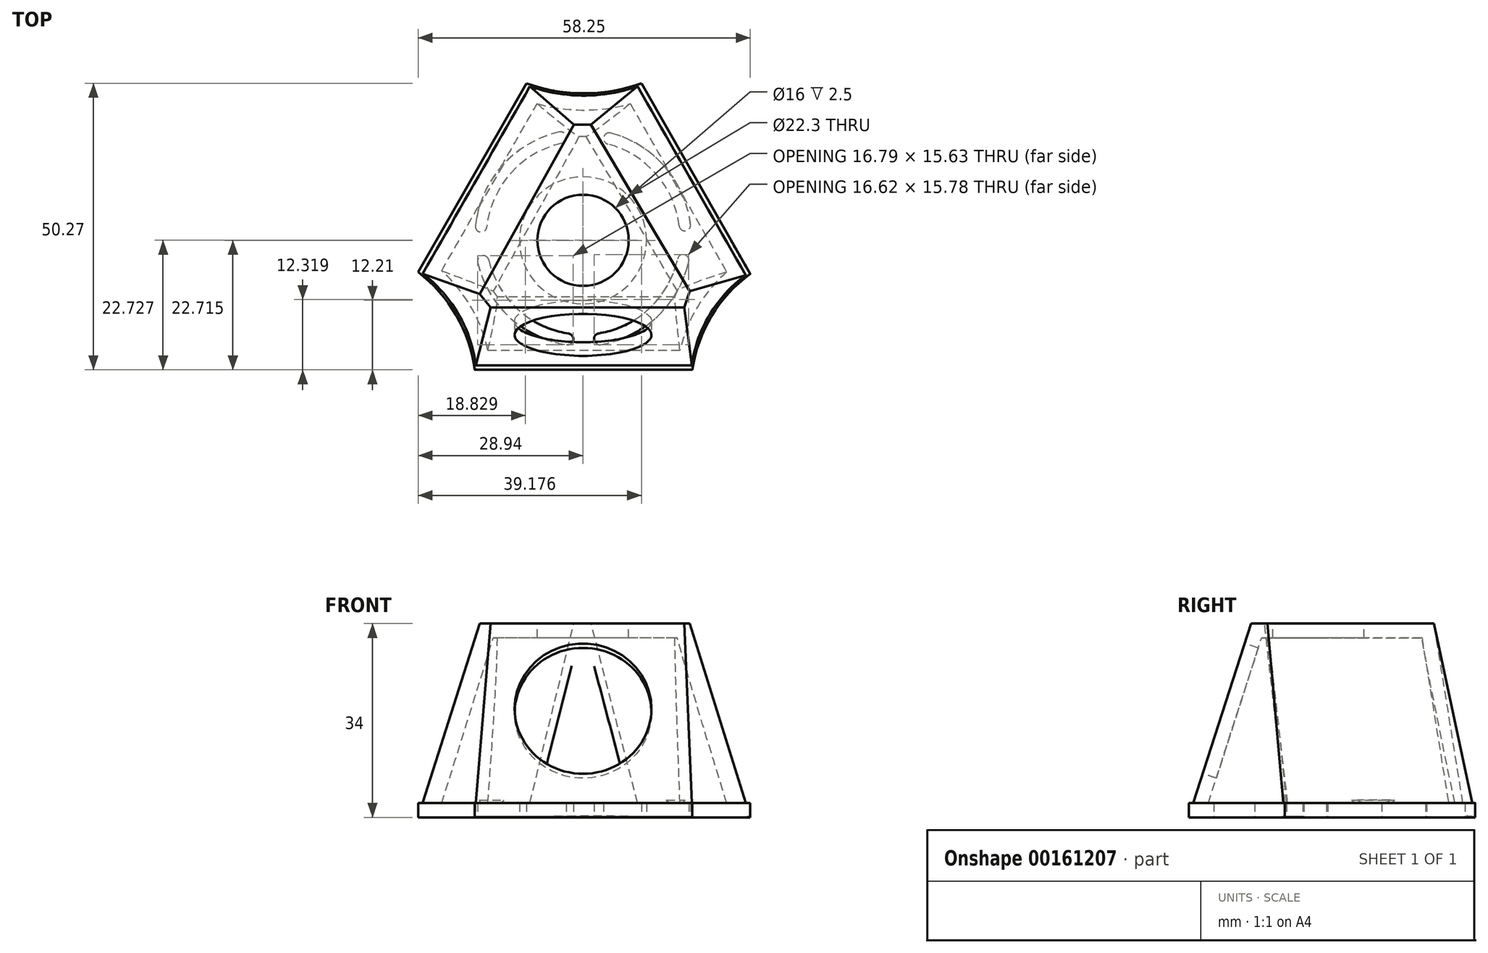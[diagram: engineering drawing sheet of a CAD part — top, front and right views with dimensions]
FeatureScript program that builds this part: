
annotation { "Feature Type Name" : "Feature", "Feature Type Description" : "" }
export const myFeature = defineFeature(function(context is Context, id is Id, definition is map)
    precondition{}
    {
        {
            var Q0;
            Q0=qCreatedBy(makeId("Top.planeOp"),FACE);
            cPlane(context, id + "F0", {"entities" : qUnion([Q0]), "cplaneType" : CPlaneType.OFFSET, "offset" : 34 * mm, "width" : 150 * mm, "height" : 150 * mm});
        }
        {
            var Q0;
            Q0=qCreatedBy(makeId("Top.planeOp"),FACE);
            var sketch = newSketch(context, id + "F1", { "sketchPlane" : qUnion([Q0])});
            skLineSegment(sketch, "E0", {"start": v(-28.93, -4.72) * mm, "end": v(-9.95, 28.39) * mm});
            skLineSegment(sketch, "E1", {"start": v(10.22, 28.39) * mm, "end": v(29.31, -5.05) * mm});
            skLineSegment(sketch, "E2", {"start": v(19.17, -21.87) * mm, "end": v(-19, -21.87) * mm});
            skArc(sketch, "E3", {"start": v(-9.95, 28.39) * mm, "mid": v(0.14, 26.64) * mm, "end": v(10.22, 28.39) * mm});
            skArc(sketch, "E4", {"start": v(-19, -21.87) * mm, "mid": v(-22.22, -12.29) * mm, "end": v(-28.93, -4.72) * mm});
            skArc(sketch, "E5", {"start": v(29.31, -5.05) * mm, "mid": v(22.5, -12.41) * mm, "end": v(19.17, -21.87) * mm});
            skSolve(sketch);
        }
        {
            var Q0;
            Q0=qCreatedBy(id+"F0.planeOp",FACE);
            var sketch = newSketch(context, id + "F2", { "sketchPlane" : qUnion([Q0])});
            skLineSegment(sketch, "E6", {"start": v(-18.1, -8.57) * mm, "end": v(-1.61, 21.16) * mm});
            skLineSegment(sketch, "E7", {"start": v(-1.61, 21.16) * mm, "end": v(1.39, 21.16) * mm});
            skLineSegment(sketch, "E8", {"start": v(1.39, 21.16) * mm, "end": v(18.72, -8.08) * mm});
            skLineSegment(sketch, "E9", {"start": v(18.72, -8.08) * mm, "end": v(17.75, -10.92) * mm});
            skLineSegment(sketch, "E10", {"start": v(17.75, -10.92) * mm, "end": v(-16.25, -10.92) * mm});
            skLineSegment(sketch, "E11", {"start": v(-16.25, -10.92) * mm, "end": v(-18.1, -8.57) * mm});
            skSolve(sketch);
        }
        {
            var Q0;
            Q0=makeQuery(id+"F1.imprint","IMPRINT",FACE,{"disambiguationData":[TD([[makeQuery(id+"F1.imprint","IMPRINT",EDGE,{"derivedFrom":sQuery(id+"F1.wireOp",EDGE,"E0")}),-1.0]])]});
            var Q1;
            Q1=makeQuery(id+"F2.imprint","IMPRINT",FACE,{"disambiguationData":[TD([[makeQuery(id+"F2.imprint","IMPRINT",EDGE,{"derivedFrom":sQuery(id+"F2.wireOp",EDGE,"E6")}),-1.0]])]});
            loft(context, id + "F3", {"sheetProfilesArray" : [{ "sheetProfileEntities" : qUnion([Q0]) }, { "sheetProfileEntities" : qUnion([Q1]) }]});
        }
        {
            var Q0;
            Q0=makeQuery(id+"F3.opLoft","CAP_FACE",FACE,{"disambiguationData":[OSD([makeQuery(id+"F1.imprint","IMPRINT",FACE,{"disambiguationData":[TD([[makeQuery(id+"F1.imprint","IMPRINT",EDGE,{"derivedFrom":sQuery(id+"F1.wireOp",EDGE,"E0")}),-1.0]])]})])],"isStart":true});
            shell(context, id + "F4", {"entities" : qUnion([Q0]), "thickness" : 2.5 * mm});
        }
        {
            var Q0;
            Q0=qCreatedBy(makeId("Top.planeOp"),FACE);
            var sketch = newSketch(context, id + "F5", { "sketchPlane" : qUnion([Q0])});
            skCircle(sketch, "E12", {"center": v(0, 0.84) * mm, "radius": 11.15 * mm});
            skSolve(sketch);
        }
        {
            var Q0;
            Q0=qCreatedBy(id+"F0.planeOp",FACE);
            var sketch = newSketch(context, id + "F6", { "sketchPlane" : qUnion([Q0])});
            skCircle(sketch, "E13", {"center": v(0, 0.86) * mm, "radius": 8 * mm});
            skSolve(sketch);
        }
        {
            var Q0;
            Q0 = qSketchRegion(id + "F6", true);
            extrude(context, id + "F7", {"entities" : qUnion([Q0]), "operationType" : NewBodyOperationType.REMOVE, "endBound" : BoundingType.UP_TO_NEXT, "oppositeDirection" : true, "depth" : 25 * mm});
        }
        {
            var Q0;
            Q0=qCreatedBy(makeId("Top.planeOp"),FACE);
            var sketch = newSketch(context, id + "F8", { "sketchPlane" : qUnion([Q0])});
            skLineSegment(sketch, "E14", {"start": v(-28.94, -4.72) * mm, "end": v(-9.95, 28.4) * mm});
            skLineSegment(sketch, "E15", {"start": v(10.24, 28.39) * mm, "end": v(29.3, -5.04) * mm});
            skLineSegment(sketch, "E16", {"start": v(19.17, -21.86) * mm, "end": v(-19, -21.86) * mm});
            skArc(sketch, "E17", {"start": v(-9.95, 28.4) * mm, "mid": v(0.14, 26.6) * mm, "end": v(10.24, 28.39) * mm});
            skArc(sketch, "E18", {"start": v(-19, -21.86) * mm, "mid": v(-22.26, -12.3) * mm, "end": v(-28.94, -4.72) * mm});
            skArc(sketch, "E19", {"start": v(29.3, -5.04) * mm, "mid": v(22.54, -12.43) * mm, "end": v(19.17, -21.86) * mm});
            skSolve(sketch);
        }
        {
            var Q0;
            Q0 = qSketchRegion(id + "F8", true);
            extrude(context, id + "F9", {"entities" : qUnion([Q0]), "operationType" : NewBodyOperationType.ADD, "depth" : 2.5 * mm});
        }
        {
            var Q0;
            Q0 = qSketchRegion(id + "F5", true);
            extrude(context, id + "F10", {"entities" : qUnion([Q0]), "operationType" : NewBodyOperationType.REMOVE, "endBound" : BoundingType.UP_TO_NEXT, "depth" : 25 * mm});
        }
        {
            var Q0;
            Q0=qCreatedBy(makeId("Top.planeOp"),FACE);
            var sketch = newSketch(context, id + "F11", { "sketchPlane" : qUnion([Q0])});
            skArc(sketch, "E20", {"start": v(-3.7, 17.9) * mm, "mid": v(-12.66, 12.65) * mm, "end": v(-16.9, 3.18) * mm});
            skArc(sketch, "E21", {"start": v(-4.15, 19.85) * mm, "mid": v(-14.15, 13.98) * mm, "end": v(-18.88, 3.4) * mm});
            skArc(sketch, "E22", {"start": v(-2.86, -17.48) * mm, "mid": v(-1.72, -16.64) * mm, "end": v(-2.56, -15.5) * mm});
            skArc(sketch, "E23", {"start": v(2.75, -15.47) * mm, "mid": v(1.93, -16.62) * mm, "end": v(3.07, -17.44) * mm});
            skArc(sketch, "E24", {"start": v(-16.55, -2.6) * mm, "mid": v(-17.75, -1.86) * mm, "end": v(-18.5, -3.06) * mm});
            skArc(sketch, "E25", {"start": v(-18.88, 3.4) * mm, "mid": v(-18, 2.3) * mm, "end": v(-16.9, 3.18) * mm});
            skArc(sketch, "E26", {"start": v(18.54, -2.86) * mm, "mid": v(17.78, -1.67) * mm, "end": v(16.59, -2.42) * mm});
            skArc(sketch, "E27", {"start": v(16.87, 3.38) * mm, "mid": v(17.99, 2.51) * mm, "end": v(18.86, 3.63) * mm});
            skArc(sketch, "E28", {"start": v(-3.7, 17.9) * mm, "mid": v(-2.95, 19.1) * mm, "end": v(-4.15, 19.85) * mm});
            skArc(sketch, "E29", {"start": v(4.85, 19.68) * mm, "mid": v(3.63, 18.97) * mm, "end": v(4.34, 17.74) * mm});
            skArc(sketch, "E30.trimOffspring", {"start": v(16.87, 3.38) * mm, "mid": v(12.8, 12.49) * mm, "end": v(4.34, 17.74) * mm});
            skArc(sketch, "E31.trimOffspring", {"start": v(18.86, 3.63) * mm, "mid": v(14.31, 13.8) * mm, "end": v(4.85, 19.68) * mm});
            skArc(sketch, "E32.trimOffspring", {"start": v(2.75, -15.47) * mm, "mid": v(11.66, -11.06) * mm, "end": v(16.59, -2.42) * mm});
            skArc(sketch, "E33.trimOffspring", {"start": v(3.07, -17.44) * mm, "mid": v(13.03, -12.52) * mm, "end": v(18.54, -2.86) * mm});
            skArc(sketch, "E34.trimOffspring", {"start": v(-16.55, -2.6) * mm, "mid": v(-11.52, -11.2) * mm, "end": v(-2.56, -15.5) * mm});
            skArc(sketch, "E35.trimOffspring", {"start": v(-18.5, -3.06) * mm, "mid": v(-12.88, -12.66) * mm, "end": v(-2.86, -17.48) * mm});
            skSolve(sketch);
        }
        {
            var Q0;
            Q0 = qSketchRegion(id + "F11", true);
            extrude(context, id + "F12", {"entities" : qUnion([Q0]), "operationType" : NewBodyOperationType.REMOVE, "depth" : 3 * mm});
        }
        {
            var Q0;
            {var subQ0=sQuery(id+"F2.wireOp",EDGE,"E11");var subQ1=sQuery(id+"F2.wireOp",EDGE,"E10");var subQ2=sQuery(id+"F2.wireOp",EDGE,"E6");var subQ3=sQuery(id+"F1.wireOp",EDGE,"E4");var subQ4=sQuery(id+"F1.wireOp",EDGE,"E2");var subQ5=sQuery(id+"F2.wireOp",EDGE,"E9");var subQ7=sQuery(id+"F1.wireOp",EDGE,"E5");Q0=makeQuery(id+"F9.boolean.opBoolean","SPLIT",FACE,{"disambiguationData":[TD([makeQuery(id+"F3.opLoft","CAP_FACE",FACE,{"disambiguationData":[OSD([makeQuery(id+"F2.imprint","IMPRINT",FACE,{"disambiguationData":[TD([[makeQuery(id+"F2.imprint","IMPRINT",EDGE,{"derivedFrom":subQ2}),-1.0]])]})])],"isStart":true})])],"derivedFrom":makeQuery(id+"F3.opLoft","SWEPT_FACE",FACE,{"disambiguationData":[OSD([subQ4,subQ3,subQ7,subQ5,subQ1,subQ0])]})});}
            cPlane(context, id + "F13", {"entities" : qUnion([Q0]), "cplaneType" : CPlaneType.OFFSET, "offset" : 0 * mm, "width" : 150 * mm, "height" : 150 * mm});
        }
        {
            var Q0;
            Q0=qCreatedBy(id+"F13.planeOp",FACE);
            var sketch = newSketch(context, id + "F14", { "sketchPlane" : qUnion([Q0])});
            skCircle(sketch, "E36", {"center": v(0, 13.33) * mm, "radius": 12 * mm});
            skSolve(sketch);
        }
        {
            var Q0;
            Q0 = qSketchRegion(id + "F14", true);
            extrude(context, id + "F15", {"entities" : qUnion([Q0]), "operationType" : NewBodyOperationType.REMOVE, "endBound" : BoundingType.UP_TO_NEXT, "oppositeDirection" : true, "depth" : 25 * mm});
        }
    });
